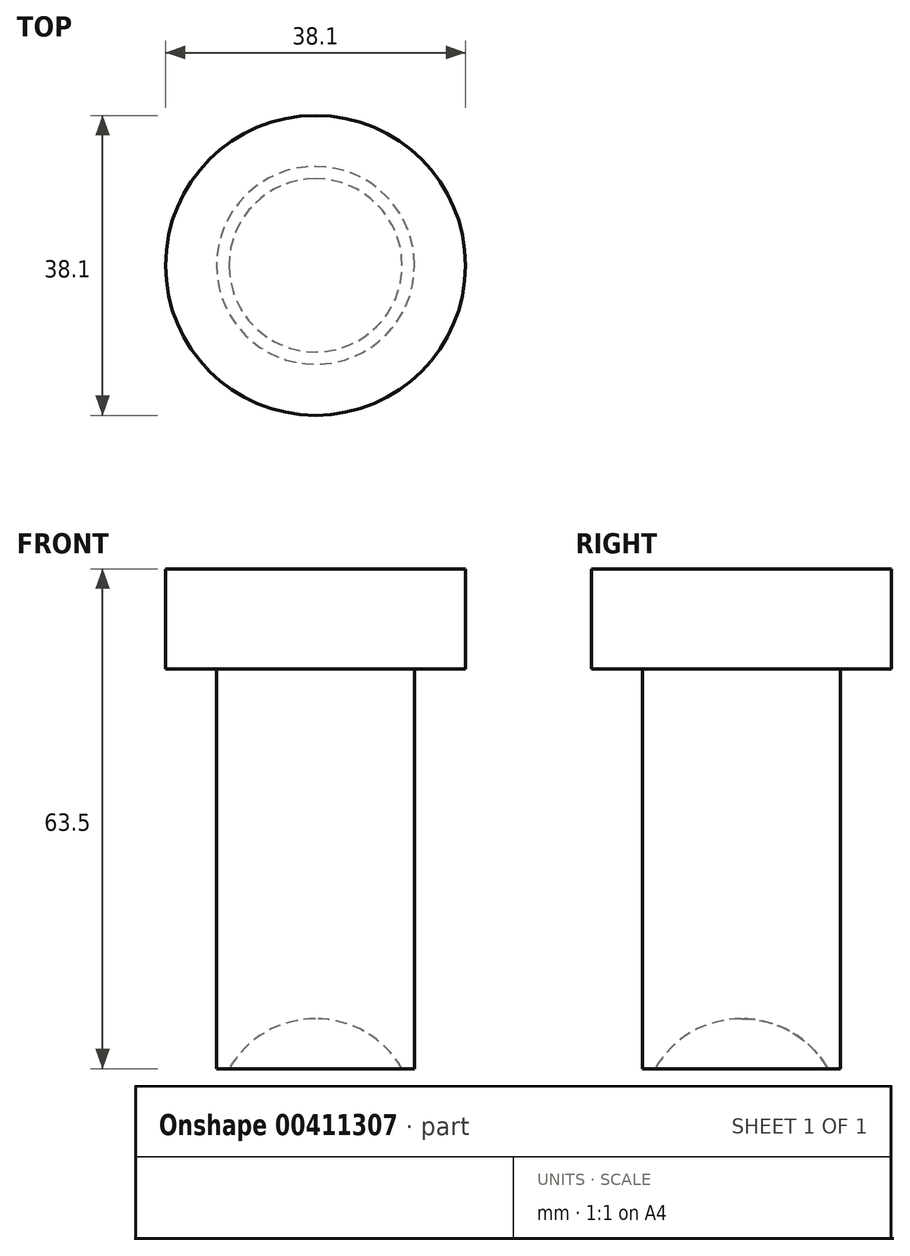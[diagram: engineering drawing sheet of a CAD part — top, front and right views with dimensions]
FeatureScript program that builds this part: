
annotation { "Feature Type Name" : "Feature", "Feature Type Description" : "" }
export const myFeature = defineFeature(function(context is Context, id is Id, definition is map)
    precondition{}
    {
        {
            var Q0;
            Q0=qCreatedBy(makeId("Top.planeOp"),FACE);
            var sketch = newSketch(context, id + "F0", { "sketchPlane" : qUnion([Q0])});
            skCircle(sketch, "E0", {"center": v(0, 0) * mm, "radius": 19.05 * mm});
            skSolve(sketch);
        }
        {
            var Q0;
            Q0=makeQuery(id+"F0.imprint","IMPRINT",FACE,{"disambiguationData":[TD([[makeQuery(id+"F0.imprint","IMPRINT",EDGE,{"derivedFrom":sQuery(id+"F0.wireOp",EDGE,"E0")}),1.0]])]});
            extrude(context, id + "F1", {"entities" : qUnion([Q0]), "depth" : 12.7 * mm});
        }
        {
            var Q0;
            Q0=makeQuery(id+"F1.opExtrude","CAP_FACE",FACE,{"disambiguationData":[OSD([sQuery(id+"F0.wireOp",EDGE,"E0")])],"isStart":true});
            var sketch = newSketch(context, id + "F2", { "sketchPlane" : qUnion([Q0])});
            skCircle(sketch, "E1", {"center": v(0, 0) * mm, "radius": 12.57 * mm});
            skSolve(sketch);
        }
        {
            var Q0;
            Q0=makeQuery(id+"F2.imprint","IMPRINT",FACE,{"disambiguationData":[TD([[makeQuery(id+"F2.imprint","IMPRINT",EDGE,{"derivedFrom":sQuery(id+"F2.wireOp",EDGE,"E1")}),1.0]])]});
            extrude(context, id + "F3", {"entities" : qUnion([Q0]), "operationType" : NewBodyOperationType.ADD, "depth" : 50.8 * mm});
        }
        {
            var Q0;
            Q0=qCreatedBy(makeId("Right.planeOp"),FACE);
            var sketch = newSketch(context, id + "F4", { "sketchPlane" : qUnion([Q0])});
            skLineSegment(sketch, "E2", {"start": v(0, 0) * mm, "end": v(0, -57.15) * mm, "construction": true});
            skLineSegment(sketch, "E3", {"start": v(0, -57.15) * mm, "end": v(0, -82.55) * mm, "construction": true});
            skArc(sketch, "E4", {"start": v(0, -44.45) * mm, "mid": v(-12.7, -57.15) * mm, "end": v(0, -69.85) * mm});
            skLineSegment(sketch, "E5", {"start": v(-11.22, -51.2) * mm, "end": v(0, -51.2) * mm});
            skLineSegment(sketch, "E6", {"start": v(0, -51.2) * mm, "end": v(0, -44.45) * mm});
            skSolve(sketch);
        }
        {
            var Q0;
            Q0 = qSketchRegion(id + "F4", true);
            var Q1;
            Q1=sQuery(id+"F4.wireOp",EDGE,"E2");
            revolve(context, id + "F5", {"operationType" : NewBodyOperationType.REMOVE, "entities" : qUnion([Q0]), "axis" : qUnion([Q1]), "revolveType" : RevolveType.FULL, "oppositeDirection" : true});
        }
    });
